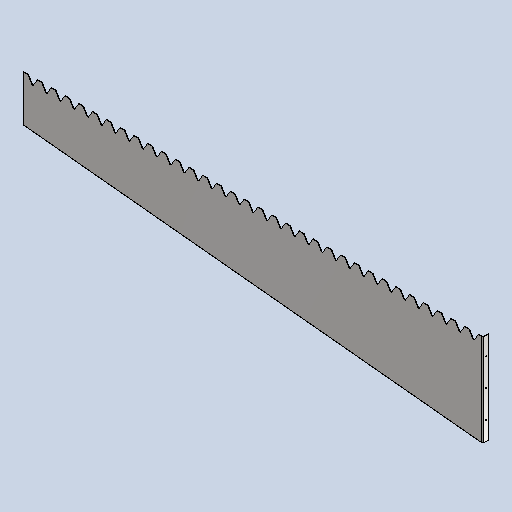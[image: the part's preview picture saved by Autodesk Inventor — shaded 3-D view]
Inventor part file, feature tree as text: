
AUTODESK INVENTOR PART (.ipt)
format: ipt  version: 2025 (Build 290162010, 162A)  size: 616,448 bytes
history: native  units: mm
features: other x6, sheet_metal_op x4, sketch x4, reference x3, extrude x2, fillet x1, pattern_linear x1
ambient origin geometry x8: Origin, YZ Plane, XZ Plane, XY Plane, X Axis, Y Axis, Z Axis, Center Point
bodies: Solid1 (feature_tree)
feature tree (21):
  sheet_metal_op  "Face1"
  extrude  "Extrusion2"  Depth=2000.0mm
  fillet  "Fillet2"  Radius=200.0mm
  pattern_linear  "Rectangular Pattern1"  Count1=4  [1 undecoded]
  sheet_metal_op  "Flange1"
  extrude  "Extrusion3"  Depth=30.0mm
  other  "A-Side Definition"
  sketch  "Sketch1"  dims[d0=400.0mm d1=2000.0mm d2=200.0mm]
  other  "Plate1"
  sketch  "Sketch3"  dims[d3=2.0mm]
  sketch  "Sketch4"  dims[d4=10.0mm]
  other  "Plate2"
  sheet_metal_op  "Bend1"
  sheet_metal_op  "Corner1"
  sketch  "Sketch6"  dims[d12=5.0mm d13=40.0mm d14=30.0mm d15=20.0mm d16=0.0mm d17=0.0mm d18=2.0mm d19=330.0mm d21=60.0mm d22=2.0mm d23=1.0mm d24=4.0mm d25=2.75mm d26=25.0mm d27=90.0deg d28=2.75mm d29=8.0mm d30=2.0mm d31=2.75mm d36=0.0mm d37=0.0mm]
  reference  "Reference2"
  reference  "Reference3"
  reference  "Reference4"
  other  "ASY MSC 001 отстойник осветлитель.iam"
  other  "MSC 705 ridge 3.ipt:1"
  other  "Definition1"
note: 1 required parameter value undecoded (feature->parameter linkage not recoverable at this tier; creation-order binding heuristic only, values carry confidence <= 0.55)
